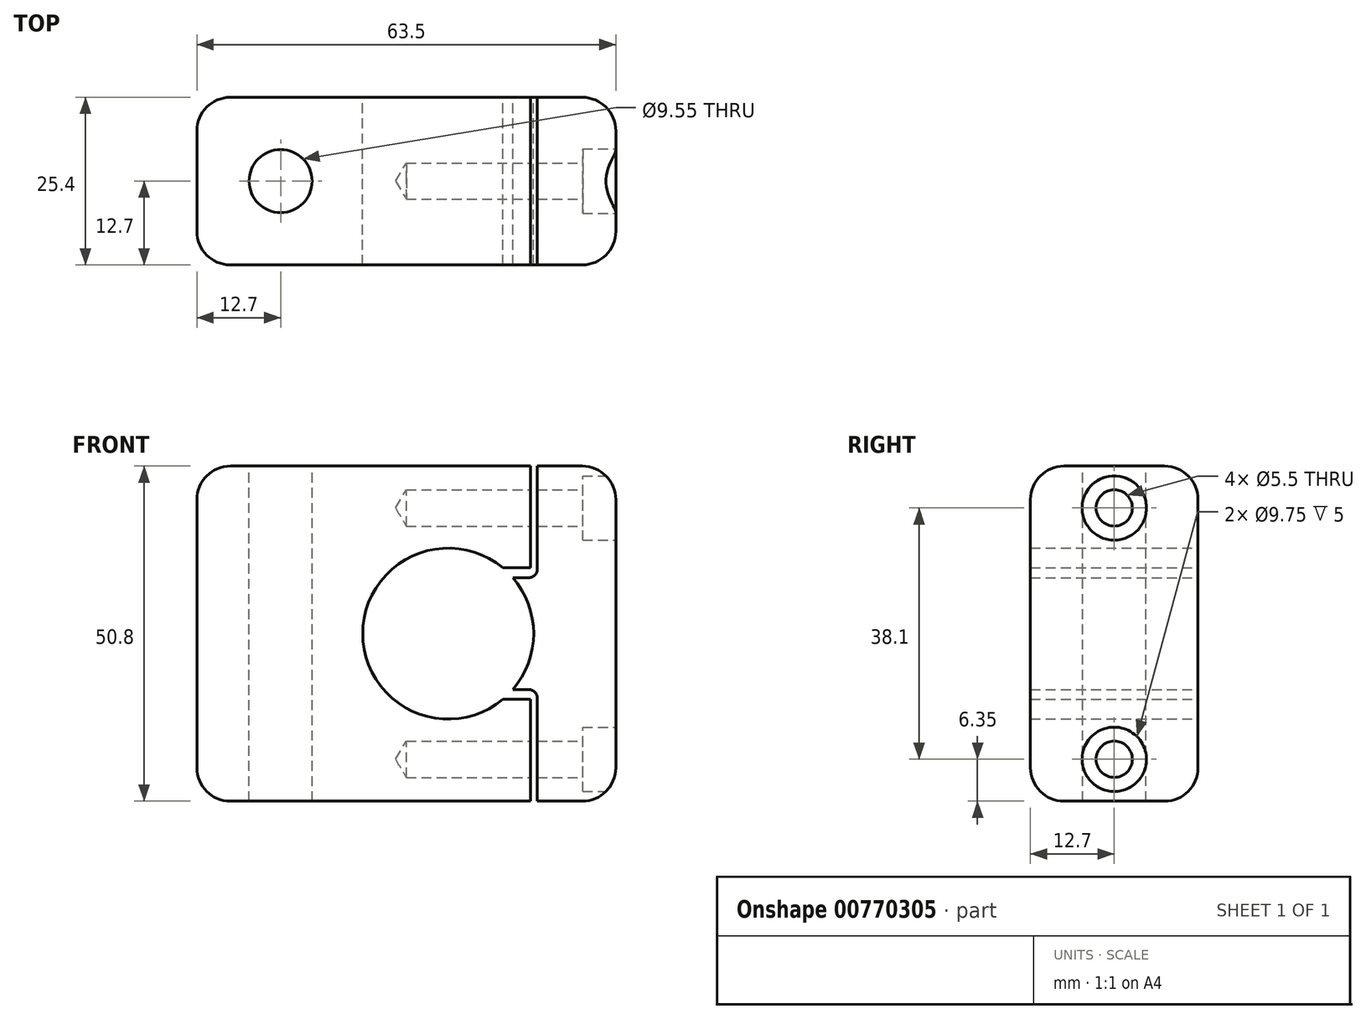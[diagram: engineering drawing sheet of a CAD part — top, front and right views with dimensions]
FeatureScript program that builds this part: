
annotation { "Feature Type Name" : "Feature", "Feature Type Description" : "" }
export const myFeature = defineFeature(function(context is Context, id is Id, definition is map)
    precondition{}
    {
        {
            var Q0;
            Q0=qCreatedBy(makeId("Front.planeOp"),FACE);
            var sketch = newSketch(context, id + "F0", { "sketchPlane" : qUnion([Q0])});
            skCircle(sketch, "E0", {"center": v(0, 0) * mm, "radius": 12.95 * mm, "construction": true});
            skSolve(sketch);
        }
        {
            var Q0;
            Q0=qCreatedBy(makeId("Front.planeOp"),FACE);
            var sketch = newSketch(context, id + "F1", { "sketchPlane" : qUnion([Q0])});
            skArc(sketch, "E1.0", {"start": v(8.28, 9.96) * mm, "mid": v(-12.95, 0) * mm, "end": v(8.28, -9.96) * mm});
            skLineSegment(sketch, "E2.bottom", {"start": v(-38.1, 25.4) * mm, "end": v(12.05, 25.4) * mm});
            skLineSegment(sketch, "E2.top", {"start": v(-38.1, -25.4) * mm, "end": v(12.5, -25.4) * mm});
            skLineSegment(sketch, "E2.left", {"start": v(-38.1, 25.4) * mm, "end": v(-38.1, -25.4) * mm});
            skLineSegment(sketch, "E2.right", {"start": v(25.4, 25.4) * mm, "end": v(25.4, -25.4) * mm});
            skLineSegment(sketch, "E3", {"start": v(9.78, 8.5) * mm, "end": v(12.23, 8.5) * mm});
            skLineSegment(sketch, "E4", {"start": v(13.5, 9.76) * mm, "end": v(13.5, 25.4) * mm});
            skLineSegment(sketch, "E5", {"start": v(8.28, 9.96) * mm, "end": v(12.5, 9.96) * mm});
            skLineSegment(sketch, "E6.trimOffspring", {"start": v(13.5, 25.4) * mm, "end": v(25.4, 25.4) * mm});
            skPoint(sketch, "E7.visualSharp", {"position": v(13.5, 8.5) * mm});
            skArc(sketch, "E7.filletArc", {"start": v(12.23, 8.5) * mm, "mid": v(13.13, 8.86) * mm, "end": v(13.5, 9.76) * mm});
            skLineSegment(sketch, "E8", {"start": v(12.05, 25.4) * mm, "end": v(12.5, 25.4) * mm});
            skLineSegment(sketch, "E9.MirrorCS", {"start": v(8.28, -9.96) * mm, "end": v(12.5, -9.96) * mm});
            skLineSegment(sketch, "E10.MirrorCS", {"start": v(13.5, -9.76) * mm, "end": v(13.5, -25.4) * mm});
            skLineSegment(sketch, "E11.MirrorCS", {"start": v(9.78, -8.5) * mm, "end": v(12.23, -8.5) * mm});
            skArc(sketch, "E12.MirrorCS", {"start": v(12.23, -8.5) * mm, "mid": v(13.13, -8.86) * mm, "end": v(13.5, -9.76) * mm});
            skArc(sketch, "E13.trimOffspring", {"start": v(9.78, -8.5) * mm, "mid": v(12.95, 0) * mm, "end": v(9.78, 8.5) * mm});
            skLineSegment(sketch, "E14", {"start": v(12.5, 25.4) * mm, "end": v(12.5, 9.96) * mm});
            skLineSegment(sketch, "E15.MirrorCS", {"start": v(12.5, -25.4) * mm, "end": v(12.5, -9.96) * mm});
            skPoint(sketch, "E16.orphan", {"position": v(13.5, 9.96) * mm});
            skPoint(sketch, "E17.orphan", {"position": v(13.5, -9.96) * mm});
            skLineSegment(sketch, "E18.trimOffspring", {"start": v(13.5, -25.4) * mm, "end": v(25.4, -25.4) * mm});
            skSolve(sketch);
        }
        {
            var Q0;
            Q0 = qSketchRegion(id + "F1", true);
            extrude(context, id + "F2", {"entities" : qUnion([Q0]), "depth" : 25.4 * mm, "offsetDistance" : 25.4 * mm});
        }
        {
            var Q0;
            Q0=makeQuery(id+"F2.opExtrude","SWEPT_FACE",FACE,{"disambiguationData":[OSD([sQuery(id+"F1.wireOp",EDGE,"E2.bottom"),sQuery(id+"F1.wireOp",EDGE,"E8")])]});
            var sketch = newSketch(context, id + "F3", { "sketchPlane" : qUnion([Q0])});
            skPoint(sketch, "E19", {"position": v(-25.4, -12.7) * mm});
            skSolve(sketch);
        }
        {
            var Q0;
            Q0=makeQuery(id+"F2.opExtrude","SWEPT_FACE",FACE,{"disambiguationData":[OSD([sQuery(id+"F1.wireOp",EDGE,"E2.right")])]});
            var sketch = newSketch(context, id + "F4", { "sketchPlane" : qUnion([Q0])});
            skPoint(sketch, "E20", {"position": v(-12.7, 19.05) * mm});
            skPoint(sketch, "E21.MirrorP", {"position": v(-12.7, -19.05) * mm});
            skSolve(sketch);
        }
        {
            var Q0;
            Q0=sQuery(id+"F4.wireOp",VERTEX,"E20");
            var Q1;
            Q1=sQuery(id+"F4.wireOp",VERTEX,"E21.MirrorP");
            var Q2;
            Q2=makeQuery(id+"F2.opExtrude","SWEPT_BODY",BODY,{"disambiguationData":[OSD([sQuery(id+"F1.wireOp",EDGE,"E1.0"),sQuery(id+"F1.wireOp",EDGE,"E2.bottom"),sQuery(id+"F1.wireOp",EDGE,"E2.top"),sQuery(id+"F1.wireOp",EDGE,"E2.left"),sQuery(id+"F1.wireOp",EDGE,"E5"),sQuery(id+"F1.wireOp",EDGE,"E8"),sQuery(id+"F1.wireOp",EDGE,"E9.MirrorCS"),sQuery(id+"F1.wireOp",EDGE,"E14"),sQuery(id+"F1.wireOp",EDGE,"E15.MirrorCS")])]});
            var Q3;
            Q3=makeQuery(id+"F2.opExtrude","SWEPT_BODY",BODY,{"disambiguationData":[OSD([sQuery(id+"F1.wireOp",EDGE,"E2.right"),sQuery(id+"F1.wireOp",EDGE,"E3"),sQuery(id+"F1.wireOp",EDGE,"E4"),sQuery(id+"F1.wireOp",EDGE,"E6.trimOffspring"),sQuery(id+"F1.wireOp",EDGE,"E7.filletArc"),sQuery(id+"F1.wireOp",EDGE,"E10.MirrorCS"),sQuery(id+"F1.wireOp",EDGE,"E11.MirrorCS"),sQuery(id+"F1.wireOp",EDGE,"E12.MirrorCS"),sQuery(id+"F1.wireOp",EDGE,"E13.trimOffspring"),sQuery(id+"F1.wireOp",EDGE,"E18.trimOffspring")])]});
            hole(context, id + "F5", {"style" : HoleStyle.C_BORE, "endStyle" : HoleEndStyle.BLIND, "standardTappedOrClearance" : lookupTablePath({ "standard" : "ISO", "fit" : "Normal", "size" : "M5", "type" : "Clearance" }), "standardBlindInLast" : lookupTablePath({ "fit" : "Standard", "standard" : "ISO", "size" : "M5", "type" : "Clearance" }), "holeDiameter" : 5.5 * mm, "cBoreDiameter" : 9.75 * mm, "cBoreDepth" : 5 * mm, "majorDiameter" : 5 * mm, "holeDepth" : 31.75 * mm, "isTappedThrough" : true, "tappedDepth" : 12.7 * mm, "tapClearance" : 3, "startFromSketch" : true, "locations" : qUnion([Q0, Q1]), "scope" : qUnion([Q2, Q3])});
        }
        {
            var Q0;
            Q0=sQuery(id+"F3.wireOp",VERTEX,"E19");
            var Q1;
            Q1=makeQuery(id+"F2.opExtrude","SWEPT_BODY",BODY,{"disambiguationData":[OSD([sQuery(id+"F1.wireOp",EDGE,"E1.0"),sQuery(id+"F1.wireOp",EDGE,"E2.bottom"),sQuery(id+"F1.wireOp",EDGE,"E2.top"),sQuery(id+"F1.wireOp",EDGE,"E2.left"),sQuery(id+"F1.wireOp",EDGE,"E5"),sQuery(id+"F1.wireOp",EDGE,"E8"),sQuery(id+"F1.wireOp",EDGE,"E9.MirrorCS"),sQuery(id+"F1.wireOp",EDGE,"E14"),sQuery(id+"F1.wireOp",EDGE,"E15.MirrorCS")])]});
            hole(context, id + "F6", {"style" : HoleStyle.SIMPLE, "endStyle" : HoleEndStyle.THROUGH, "holeDiameter" : 9.55 * mm, "majorDiameter" : 6.35 * mm, "isTappedThrough" : true, "tappedDepth" : 12.7 * mm, "tapClearance" : 3, "startFromSketch" : true, "locations" : qUnion([Q0]), "scope" : qUnion([Q1])});
        }
        {
            var Q0;
            Q0=makeQuery(id+"F2.opExtrude","SWEPT_FACE",FACE,{"disambiguationData":[OSD([sQuery(id+"F1.wireOp",EDGE,"E2.left")])]});
            var Q1;
            Q1=makeQuery(id+"F2.opExtrude","CAP_EDGE",EDGE,{"disambiguationData":[OSD([sQuery(id+"F1.wireOp",EDGE,"E2.top")])],"isStart":true});
            var Q2;
            Q2=makeQuery(id+"F2.opExtrude","CAP_EDGE",EDGE,{"disambiguationData":[OSD([sQuery(id+"F1.wireOp",EDGE,"E2.bottom"),sQuery(id+"F1.wireOp",EDGE,"E8")])],"isStart":true});
            var Q3;
            Q3=makeQuery(id+"F2.opExtrude","CAP_EDGE",EDGE,{"disambiguationData":[OSD([sQuery(id+"F1.wireOp",EDGE,"E2.bottom"),sQuery(id+"F1.wireOp",EDGE,"E8")])],"isStart":false});
            var Q4;
            Q4=makeQuery(id+"F2.opExtrude","CAP_EDGE",EDGE,{"disambiguationData":[OSD([sQuery(id+"F1.wireOp",EDGE,"E2.top")])],"isStart":false});
            var Q5;
            Q5=makeQuery(id+"F2.opExtrude","CAP_EDGE",EDGE,{"disambiguationData":[OSD([sQuery(id+"F1.wireOp",EDGE,"E2.right")])],"isStart":false});
            var Q6;
            Q6=makeQuery(id+"F2.opExtrude","CAP_EDGE",EDGE,{"disambiguationData":[OSD([sQuery(id+"F1.wireOp",EDGE,"E2.right")])],"isStart":true});
            var Q7;
            Q7=makeQuery(id+"F2.opExtrude","SWEPT_EDGE",EDGE,{"disambiguationData":[OSD([sQuery(id+"F1.wireOp",EDGE,"E2.right"),sQuery(id+"F1.wireOp",EDGE,"E18.trimOffspring")])]});
            var Q8;
            Q8=makeQuery(id+"F2.opExtrude","SWEPT_EDGE",EDGE,{"disambiguationData":[OSD([sQuery(id+"F1.wireOp",EDGE,"E2.right"),sQuery(id+"F1.wireOp",EDGE,"E6.trimOffspring")])]});
            var Q9;
            Q9=makeQuery(id+"F2.opExtrude","CAP_EDGE",EDGE,{"disambiguationData":[OSD([sQuery(id+"F1.wireOp",EDGE,"E6.trimOffspring")])],"isStart":true});
            var Q10;
            Q10=makeQuery(id+"F2.opExtrude","CAP_EDGE",EDGE,{"disambiguationData":[OSD([sQuery(id+"F1.wireOp",EDGE,"E6.trimOffspring")])],"isStart":false});
            var Q11;
            Q11=makeQuery(id+"F2.opExtrude","CAP_EDGE",EDGE,{"disambiguationData":[OSD([sQuery(id+"F1.wireOp",EDGE,"E18.trimOffspring")])],"isStart":true});
            var Q12;
            Q12=makeQuery(id+"F2.opExtrude","CAP_EDGE",EDGE,{"disambiguationData":[OSD([sQuery(id+"F1.wireOp",EDGE,"E18.trimOffspring")])],"isStart":false});
            fillet(context, id + "F7", {"entities" : qUnion([Q0, Q1, Q2, Q3, Q4, Q5, Q6, Q7, Q8, Q9, Q10, Q11, Q12]), "radius" : 5.08 * mm, "tangentPropagation" : true, "allowEdgeOverflow" : false});
        }
    });
